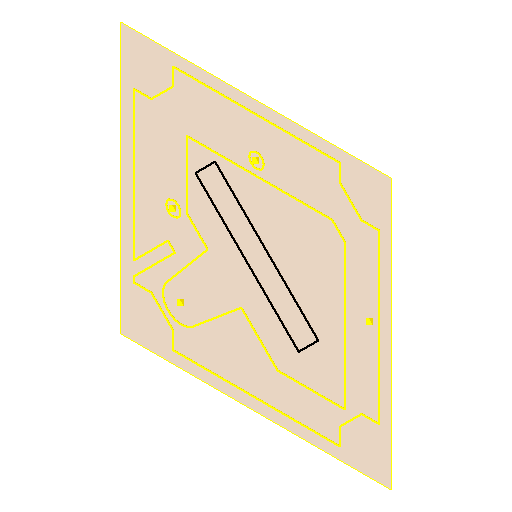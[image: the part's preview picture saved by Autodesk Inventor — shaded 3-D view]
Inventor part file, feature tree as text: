
AUTODESK INVENTOR PART (.ipt)
format: ipt  version: 2022 (Build 260153000, 153)  size: 84,992 bytes
history: native  units: in
note: dims shown in document units (in); Inventor stores cm internally (conversion verified against a paired STEP export)
features: other x3, plane x1, reference x1
ambient origin geometry x8: Origin, YZ Plane, XZ Plane, XY Plane, X Axis, Y Axis, Z Axis, Center Point
feature tree (5):
  plane  "Arbeitsebene1"
  reference  "Referenz1"
  other  "Assembly_Cube_Fibercombiner_v3.iam"
  other  "20_Cube_Insert_Fibercombiner_FPC_v3:1"
  other  "<userpath>\Dropbox\UC2\02_CAD\INVENTOR\uc2_v3\Assembly_Cube_Fibercombiner_v3.iam"
